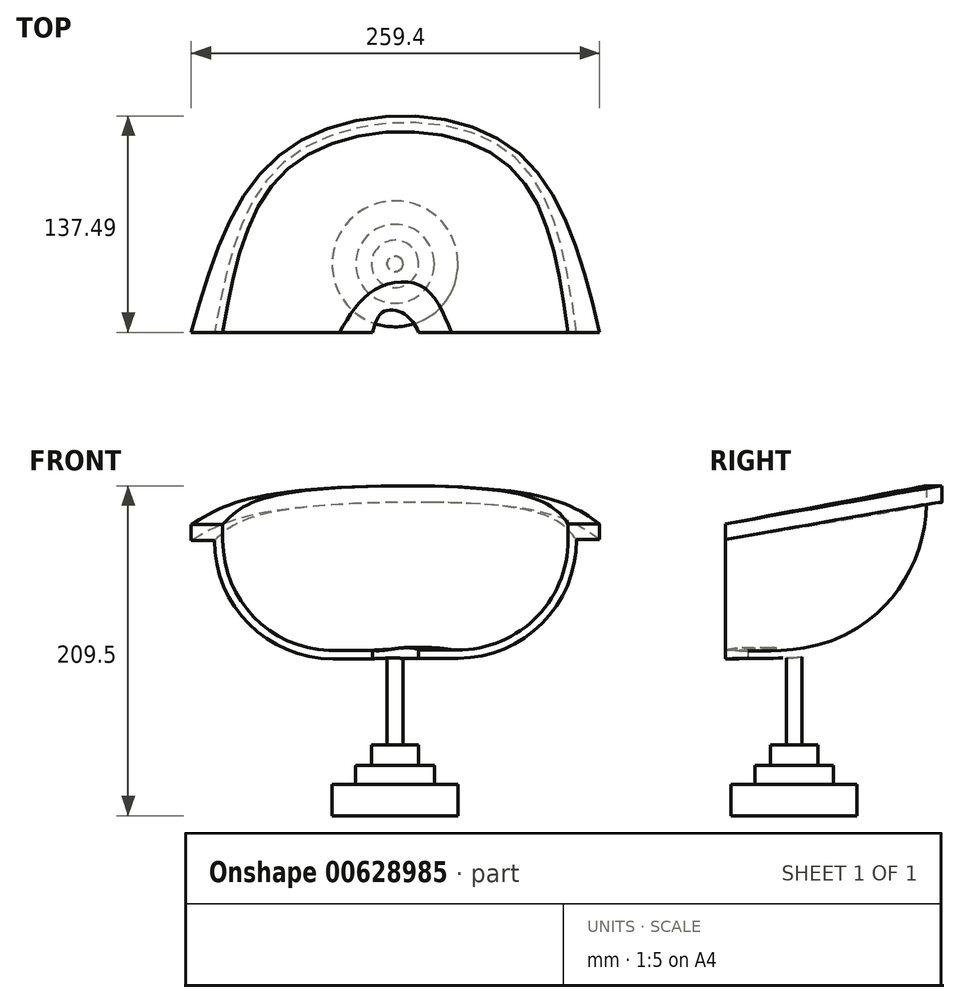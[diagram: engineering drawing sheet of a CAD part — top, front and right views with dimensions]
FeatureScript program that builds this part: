
annotation { "Feature Type Name" : "Feature", "Feature Type Description" : "" }
export const myFeature = defineFeature(function(context is Context, id is Id, definition is map)
    precondition{}
    {
        {
            var Q0;
            Q0=qCreatedBy(makeId("Front.planeOp"),FACE);
            var sketch = newSketch(context, id + "F0", { "sketchPlane" : qUnion([Q0])});
            skLineSegment(sketch, "E0.bottom", {"start": v(15, 5.41) * mm, "end": v(40, 5.41) * mm});
            skLineSegment(sketch, "E0.top", {"start": v(15, 0) * mm, "end": v(40, 0) * mm});
            skLineSegment(sketch, "E0.left", {"start": v(15, 5.41) * mm, "end": v(15, 0) * mm});
            skLineSegment(sketch, "E0.right", {"start": v(40, 5.41) * mm, "end": v(40, 5.28) * mm});
            skArc(sketch, "E1", {"start": v(40, 0) * mm, "mid": v(93.23, 22.05) * mm, "end": v(115.28, 75.28) * mm});
            skArc(sketch, "E2", {"start": v(35.79, 5.41) * mm, "mid": v(87.99, 24.32) * mm, "end": v(110, 75.28) * mm});
            skLineSegment(sketch, "E3.bottom", {"start": v(110, 85.28) * mm, "end": v(130, 85.28) * mm});
            skLineSegment(sketch, "E3.top", {"start": v(115.28, 75.28) * mm, "end": v(130, 75.28) * mm});
            skLineSegment(sketch, "E3.left", {"start": v(110, 85.28) * mm, "end": v(110, 75.28) * mm});
            skLineSegment(sketch, "E3.right", {"start": v(130, 85.28) * mm, "end": v(130, 75.28) * mm});
            skLineSegment(sketch, "E4.trimOffspring", {"start": v(40, 0) * mm, "end": v(40, 0) * mm});
            skLineSegment(sketch, "E5", {"start": v(0, 0) * mm, "end": v(0, 50) * mm});
            skSolve(sketch);
        }
        {
            var Q0;
            Q0=sQuery(id+"F0.wireOp",EDGE,"E5");
            cPlane(context, id + "F1", {"entities" : qUnion([Q0]), "cplaneType" : CPlaneType.LINE_ANGLE, "offset" : 25 * mm, "angle" : 30 * degree, "width" : 150 * mm, "height" : 150 * mm});
        }
        {
            var Q0;
            Q0=qCreatedBy(id+"F1.planeOp",FACE);
            var sketch = newSketch(context, id + "F2", { "sketchPlane" : qUnion([Q0])});
            skLineSegment(sketch, "E6.bottom", {"start": v(15, 5) * mm, "end": v(35, 5) * mm});
            skLineSegment(sketch, "E6.top", {"start": v(15, 0) * mm, "end": v(35, 0) * mm});
            skLineSegment(sketch, "E6.left", {"start": v(15, 5) * mm, "end": v(15, 0) * mm});
            skLineSegment(sketch, "E6.right", {"start": v(35, 5) * mm, "end": v(35, 4.85) * mm});
            skArc(sketch, "E7", {"start": v(35, 0) * mm, "mid": v(102.07, 27.78) * mm, "end": v(129.85, 94.85) * mm});
            skArc(sketch, "E8", {"start": v(29.78, 5) * mm, "mid": v(96.77, 29.39) * mm, "end": v(125, 94.85) * mm});
            skLineSegment(sketch, "E9.bottom", {"start": v(125, 105.75) * mm, "end": v(135, 105.75) * mm});
            skLineSegment(sketch, "E9.top", {"start": v(129.85, 94.85) * mm, "end": v(135, 94.85) * mm});
            skLineSegment(sketch, "E9.left", {"start": v(125, 105.75) * mm, "end": v(125, 94.85) * mm});
            skLineSegment(sketch, "E9.right", {"start": v(135, 105.75) * mm, "end": v(135, 94.85) * mm});
            skLineSegment(sketch, "E10.trimOffspring", {"start": v(35, 0) * mm, "end": v(35, 0) * mm});
            skLineSegment(sketch, "E11", {"start": v(0, 0) * mm, "end": v(0, 50) * mm});
            skSolve(sketch);
        }
        {
            var Q0;
            Q0=sQuery(id+"F2.wireOp",EDGE,"E11");
            cPlane(context, id + "F3", {"entities" : qUnion([Q0]), "cplaneType" : CPlaneType.LINE_ANGLE, "offset" : 25 * mm, "angle" : 30 * degree, "oppositeDirection" : true, "width" : 150 * mm, "height" : 150 * mm});
        }
        {
            var Q0;
            Q0=qCreatedBy(id+"F3.planeOp",FACE);
            var sketch = newSketch(context, id + "F4", { "sketchPlane" : qUnion([Q0])});
            skLineSegment(sketch, "E12.bottom", {"start": v(12.97, 6.74) * mm, "end": v(39.17, 6.74) * mm});
            skLineSegment(sketch, "E12.top", {"start": v(12.97, 0) * mm, "end": v(39.17, 0) * mm});
            skLineSegment(sketch, "E12.left", {"start": v(12.97, 6.74) * mm, "end": v(12.97, 0) * mm});
            skLineSegment(sketch, "E12.right", {"start": v(39.17, 6.74) * mm, "end": v(39.17, 6.58) * mm});
            skArc(sketch, "E13", {"start": v(39.17, 0) * mm, "mid": v(107.46, 28.29) * mm, "end": v(135.75, 96.58) * mm});
            skArc(sketch, "E14", {"start": v(33.76, 6.74) * mm, "mid": v(100.87, 31.05) * mm, "end": v(129.17, 96.58) * mm});
            skLineSegment(sketch, "E15.bottom", {"start": v(129.17, 106.58) * mm, "end": v(139.17, 106.58) * mm});
            skLineSegment(sketch, "E15.top", {"start": v(135.75, 96.58) * mm, "end": v(139.17, 96.58) * mm});
            skLineSegment(sketch, "E15.left", {"start": v(129.17, 106.58) * mm, "end": v(129.17, 96.58) * mm});
            skLineSegment(sketch, "E15.right", {"start": v(139.17, 106.58) * mm, "end": v(139.17, 96.58) * mm});
            skLineSegment(sketch, "E16.trimOffspring", {"start": v(39.17, 0) * mm, "end": v(39.17, 0) * mm});
            skLineSegment(sketch, "E17", {"start": v(-0.45, -0.03) * mm, "end": v(-0.45, 49.97) * mm});
            skSolve(sketch);
        }
        {
            var Q0;
            Q0=sQuery(id+"F2.wireOp",EDGE,"E11");
            cPlane(context, id + "F5", {"entities" : qUnion([Q0]), "cplaneType" : CPlaneType.LINE_ANGLE, "offset" : 25 * mm, "angle" : 90 * degree, "width" : 150 * mm, "height" : 150 * mm});
        }
        {
            var Q0;
            Q0=qCreatedBy(id+"F5.planeOp",FACE);
            var sketch = newSketch(context, id + "F6", { "sketchPlane" : qUnion([Q0])});
            skLineSegment(sketch, "E18.bottom", {"start": v(14.4, 4.98) * mm, "end": v(39.4, 4.98) * mm});
            skLineSegment(sketch, "E18.top", {"start": v(14.4, -0.43) * mm, "end": v(39.4, -0.43) * mm});
            skLineSegment(sketch, "E18.left", {"start": v(14.4, 4.98) * mm, "end": v(14.4, -0.43) * mm});
            skLineSegment(sketch, "E18.right", {"start": v(39.4, 4.98) * mm, "end": v(39.4, 4.85) * mm});
            skArc(sketch, "E19", {"start": v(39.4, -0.43) * mm, "mid": v(92.64, 21.62) * mm, "end": v(114.69, 74.85) * mm});
            skArc(sketch, "E20", {"start": v(35.2, 4.98) * mm, "mid": v(87.39, 23.89) * mm, "end": v(109.4, 74.85) * mm});
            skLineSegment(sketch, "E21.bottom", {"start": v(109.4, 84.85) * mm, "end": v(129.4, 84.85) * mm});
            skLineSegment(sketch, "E21.top", {"start": v(114.69, 74.85) * mm, "end": v(129.4, 74.85) * mm});
            skLineSegment(sketch, "E21.left", {"start": v(109.4, 84.85) * mm, "end": v(109.4, 74.85) * mm});
            skLineSegment(sketch, "E21.right", {"start": v(129.4, 84.85) * mm, "end": v(129.4, 74.85) * mm});
            skLineSegment(sketch, "E22.trimOffspring", {"start": v(39.4, -0.43) * mm, "end": v(39.4, -0.43) * mm});
            skLineSegment(sketch, "E23", {"start": v(-0.35, -0.15) * mm, "end": v(-0.35, 49.85) * mm});
            skSolve(sketch);
        }
        {
            var Q0;
            Q0=makeQuery(id+"F0.imprint","IMPRINT",FACE,{"disambiguationData":[TD([[makeQuery(id+"F0.imprint","IMPRINT",EDGE,{"derivedFrom":sQuery(id+"F0.wireOp",EDGE,"E0.top")}),1.0]])]});
            var Q1;
            Q1=makeQuery(id+"F4.imprint","IMPRINT",FACE,{"disambiguationData":[TD([[makeQuery(id+"F4.imprint","IMPRINT",EDGE,{"derivedFrom":sQuery(id+"F4.wireOp",EDGE,"E12.top")}),1.0]])]});
            var Q2;
            Q2=makeQuery(id+"F2.imprint","IMPRINT",FACE,{"disambiguationData":[TD([[makeQuery(id+"F2.imprint","IMPRINT",EDGE,{"derivedFrom":sQuery(id+"F2.wireOp",EDGE,"E7")}),1.0]])]});
            var Q3;
            Q3=makeQuery(id+"F6.imprint","IMPRINT",FACE,{"disambiguationData":[TD([[makeQuery(id+"F6.imprint","IMPRINT",EDGE,{"derivedFrom":sQuery(id+"F6.wireOp",EDGE,"E18.top")}),1.0]])]});
            loft(context, id + "F7", {"sheetProfilesArray" : [{ "sheetProfileEntities" : qUnion([Q0]) }, { "sheetProfileEntities" : qUnion([Q1]) }, { "sheetProfileEntities" : qUnion([Q2]) }, { "sheetProfileEntities" : qUnion([Q3]) }]});
        }
        {
            var Q0;
            Q0=qCreatedBy(makeId("Top.planeOp"),FACE);
            var sketch = newSketch(context, id + "F8", { "sketchPlane" : qUnion([Q0])});
            skCircle(sketch, "E24", {"center": v(0, 43.47) * mm, "radius": 5 * mm});
            skSolve(sketch);
        }
        {
            var Q0;
            Q0=makeQuery(id+"F8.imprint","IMPRINT",FACE,{"disambiguationData":[TD([[makeQuery(id+"F8.imprint","IMPRINT",EDGE,{"derivedFrom":sQuery(id+"F8.wireOp",EDGE,"E24")}),1.0]])]});
            extrude(context, id + "F9", {"entities" : qUnion([Q0]), "operationType" : NewBodyOperationType.ADD, "endBound" : BoundingType.SYMMETRIC, "oppositeDirection" : true, "depth" : 10 * mm, "offsetDistance" : 25 * mm});
        }
        {
            var Q0;
            Q0=makeQuery(id+"F9.opExtrude","CAP_FACE",FACE,{"disambiguationData":[OSD([sQuery(id+"F8.wireOp",EDGE,"E24")])],"isStart":false});
            extrude(context, id + "F10", {"entities" : qUnion([Q0]), "operationType" : NewBodyOperationType.ADD, "depth" : 70 * mm, "offsetDistance" : 25 * mm});
        }
        {
            var Q0;
            Q0=qCreatedBy(makeId("Top.planeOp"),FACE);
            cPlane(context, id + "F11", {"entities" : qUnion([Q0]), "cplaneType" : CPlaneType.OFFSET, "offset" : 80 * mm, "oppositeDirection" : true, "width" : 150 * mm, "height" : 150 * mm});
        }
        {
            var Q0;
            Q0=qCreatedBy(id+"F11.planeOp",FACE);
            var sketch = newSketch(context, id + "F12", { "sketchPlane" : qUnion([Q0])});
            skCircle(sketch, "E25", {"center": v(0, 43.47) * mm, "radius": 15 * mm});
            skSolve(sketch);
        }
        {
            var Q0;
            Q0=makeQuery(id+"F12.imprint","IMPRINT",FACE,{"disambiguationData":[TD([[makeQuery(id+"F12.imprint","IMPRINT",EDGE,{"derivedFrom":sQuery(id+"F12.wireOp",EDGE,"E25")}),1.0]])]});
            extrude(context, id + "F13", {"entities" : qUnion([Q0]), "operationType" : NewBodyOperationType.ADD, "depth" : 25 * mm, "offsetDistance" : 25 * mm});
        }
        {
            var Q0;
            Q0=qCreatedBy(id+"F11.planeOp",FACE);
            cPlane(context, id + "F14", {"entities" : qUnion([Q0]), "cplaneType" : CPlaneType.OFFSET, "offset" : 10 * mm, "oppositeDirection" : true, "width" : 150 * mm, "height" : 150 * mm});
        }
        {
            var Q0;
            Q0=qCreatedBy(id+"F14.planeOp",FACE);
            var sketch = newSketch(context, id + "F15", { "sketchPlane" : qUnion([Q0])});
            skCircle(sketch, "E26", {"center": v(0, 43.47) * mm, "radius": 25 * mm});
            skSolve(sketch);
        }
        {
            var Q0;
            Q0=makeQuery(id+"F15.imprint","IMPRINT",FACE,{"disambiguationData":[TD([[makeQuery(id+"F15.imprint","IMPRINT",EDGE,{"derivedFrom":sQuery(id+"F15.wireOp",EDGE,"E26")}),1.0]])]});
            extrude(context, id + "F16", {"entities" : qUnion([Q0]), "operationType" : NewBodyOperationType.ADD, "depth" : 22 * mm, "offsetDistance" : 25 * mm});
        }
        {
            var Q0;
            Q0=qCreatedBy(id+"F14.planeOp",FACE);
            cPlane(context, id + "F17", {"entities" : qUnion([Q0]), "cplaneType" : CPlaneType.OFFSET, "offset" : 10 * mm, "oppositeDirection" : true, "width" : 150 * mm, "height" : 150 * mm});
        }
        {
            var Q0;
            Q0=qCreatedBy(id+"F17.planeOp",FACE);
            var sketch = newSketch(context, id + "F18", { "sketchPlane" : qUnion([Q0])});
            skCircle(sketch, "E27", {"center": v(0, 43.47) * mm, "radius": 40 * mm});
            skSolve(sketch);
        }
        {
            var Q0;
            Q0=makeQuery(id+"F18.imprint","IMPRINT",FACE,{"disambiguationData":[TD([[makeQuery(id+"F18.imprint","IMPRINT",EDGE,{"derivedFrom":sQuery(id+"F18.wireOp",EDGE,"E27")}),1.0]])]});
            extrude(context, id + "F19", {"entities" : qUnion([Q0]), "operationType" : NewBodyOperationType.ADD, "depth" : 20 * mm, "offsetDistance" : 25 * mm});
        }
    });
